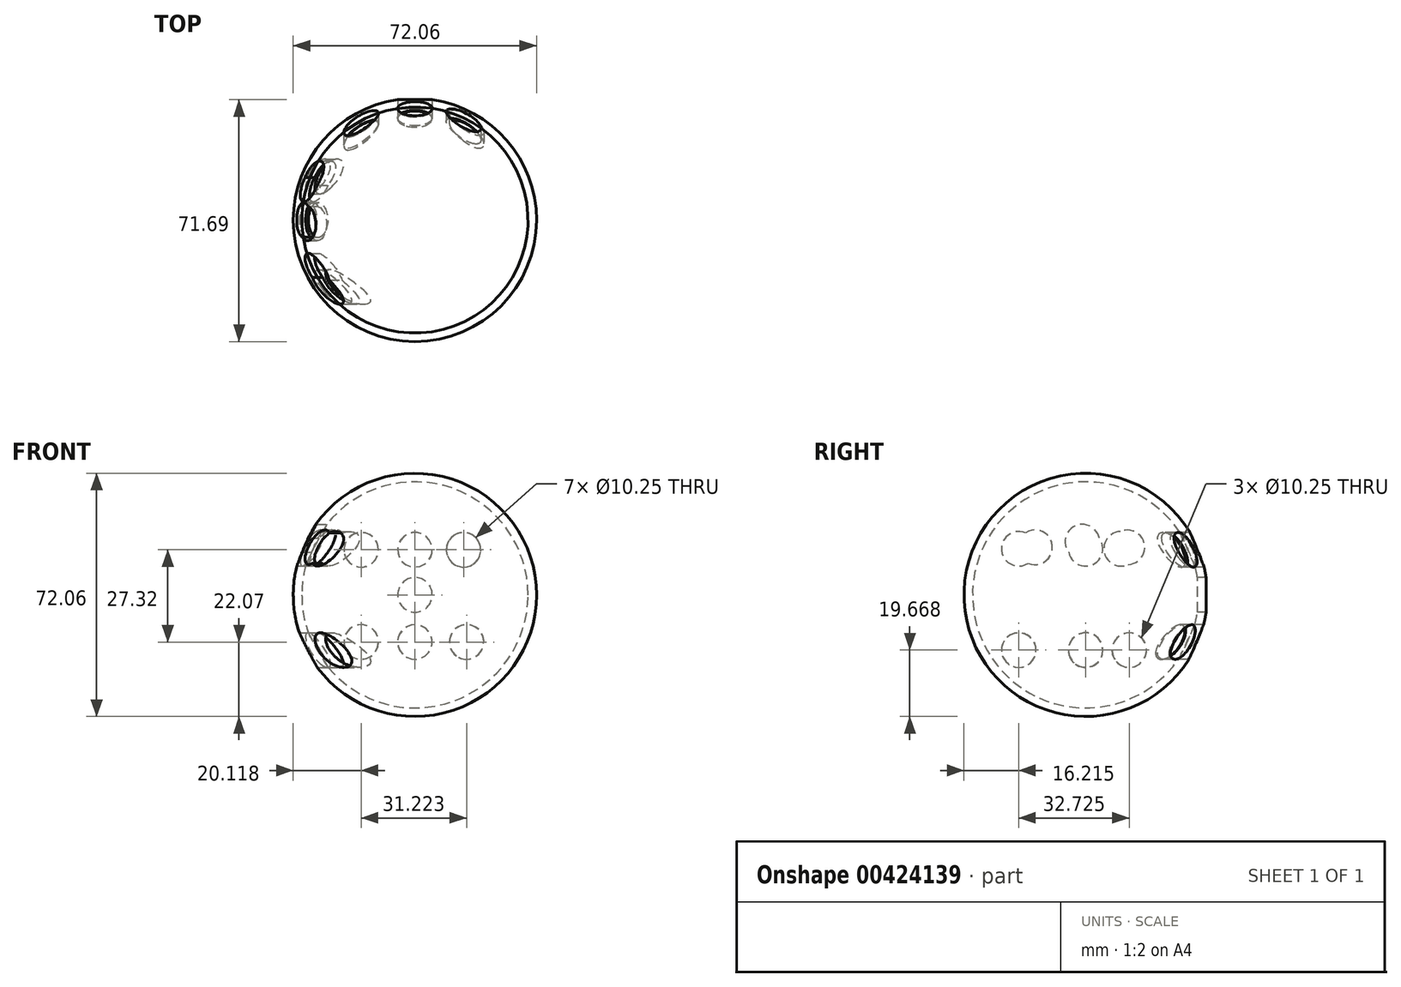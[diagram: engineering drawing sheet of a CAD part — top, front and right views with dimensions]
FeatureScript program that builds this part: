
annotation { "Feature Type Name" : "Feature", "Feature Type Description" : "" }
export const myFeature = defineFeature(function(context is Context, id is Id, definition is map)
    precondition{}
    {
        {
            var Q0;
            Q0=qCreatedBy(makeId("Front.planeOp"),FACE);
            var sketch = newSketch(context, id + "F0", { "sketchPlane" : qUnion([Q0])});
            skArc(sketch, "E0", {"start": v(-36.03, 0) * mm, "mid": v(0, -36.03) * mm, "end": v(36.03, 0) * mm});
            skLineSegment(sketch, "E1", {"start": v(-36.03, 0) * mm, "end": v(36.03, 0) * mm});
            skLineSegment(sketch, "E2", {"start": v(-57.34, 0) * mm, "end": v(54.04, 0) * mm, "construction": true});
            skSolve(sketch);
        }
        {
            var Q0;
            Q0=makeQuery(id+"F0.imprint","IMPRINT",FACE,{"disambiguationData":[TD([[makeQuery(id+"F0.imprint","IMPRINT",EDGE,{"derivedFrom":sQuery(id+"F0.wireOp",EDGE,"E0")}),1.0]])]});
            var Q1;
            Q1=sQuery(id+"F0.wireOp",EDGE,"E2");
            revolve(context, id + "F1", {"entities" : qUnion([Q0]), "axis" : qUnion([Q1]), "revolveType" : RevolveType.FULL});
        }
        {
            var Q0;
            Q0=qCreatedBy(makeId("Right.planeOp"),FACE);
            var sketch = newSketch(context, id + "F2", { "sketchPlane" : qUnion([Q0])});
            skFitSpline(sketch, "E3", {"points": [v(-56.14, 32.97) * mm, v(-60.08, 19.31) * mm, v(-56.14, 14.86) * mm, v(-52.5, 19.31) * mm, v(-56.14, 32.97) * mm]});
            skFitSpline(sketch, "E4", {"points": [v(-14.3, 24.87) * mm, v(-18.24, 11.21) * mm, v(-14.3, 6.76) * mm, v(-10.66, 11.21) * mm, v(-14.3, 24.87) * mm]});
            skFitSpline(sketch, "E5", {"points": [v(12.42, 24.87) * mm, v(8.48, 11.21) * mm, v(12.42, 6.76) * mm, v(16.06, 11.21) * mm, v(12.42, 24.87) * mm]});
            skFitSpline(sketch, "E6", {"points": [v(-0.8, 26.32) * mm, v(-4.73, 12.66) * mm, v(-0.8, 8.2) * mm, v(2.85, 12.66) * mm, v(-0.8, 26.32) * mm]});
            skPoint(sketch, "E7", {"position": v(12.35, 14.1) * mm});
            skPoint(sketch, "E8", {"position": v(-0.98, 15.77) * mm});
            skPoint(sketch, "E9", {"position": v(-14.96, 14.1) * mm});
            skSolve(sketch);
        }
        {
            var Q0;
            Q0=makeQuery(id+"F1.opRevolve","SWEPT_FACE",FACE,{"disambiguationData":[OSD([sQuery(id+"F0.wireOp",EDGE,"E0")])]});
            var Q1;
            Q1=makeQuery(id+"F1.opRevolve","SWEPT_BODY",BODY,{"disambiguationData":[OSD([sQuery(id+"F0.wireOp",EDGE,"E0"),sQuery(id+"F0.wireOp",EDGE,"E1")])]});
            shell(context, id + "F3", {"isHollow" : true, "entities" : qUnion([Q0]), "parts" : qUnion([Q1]), "thickness" : 2.54 * mm});
        }
        {
            var Q0;
            Q0=qCreatedBy(makeId("Front.planeOp"),FACE);
            var sketch = newSketch(context, id + "F4", { "sketchPlane" : qUnion([Q0])});
            skCircle(sketch, "E10", {"center": v(0, 0) * mm, "radius": 5.12 * mm});
            skSolve(sketch);
        }
        {
            var Q0;
            Q0=sQuery(id+"F4.wireOp",VERTEX,"E10.center");
            var Q1;
            Q1=makeQuery(id+"F1.opRevolve","SWEPT_BODY",BODY,{"disambiguationData":[OSD([sQuery(id+"F0.wireOp",EDGE,"E0"),sQuery(id+"F0.wireOp",EDGE,"E1")])]});
            hole(context, id + "F5", {"style" : HoleStyle.SIMPLE, "endStyle" : HoleEndStyle.THROUGH, "holeDiameter" : 10.25 * mm, "isTappedThrough" : true, "tappedDepth" : 12.7 * mm, "tapClearance" : 3, "startFromSketch" : true, "locations" : qUnion([Q0]), "scope" : qUnion([Q1])});
        }
        {
            var Q0;
            Q0=sQuery(id+"F2.wireOp",VERTEX,"E7");
            var Q1;
            Q1=sQuery(id+"F2.wireOp",VERTEX,"E8");
            var Q2;
            Q2=sQuery(id+"F2.wireOp",VERTEX,"E9");
            var Q3;
            Q3=makeQuery(id+"F1.opRevolve","SWEPT_BODY",BODY,{"disambiguationData":[OSD([sQuery(id+"F0.wireOp",EDGE,"E0"),sQuery(id+"F0.wireOp",EDGE,"E1")])]});
            hole(context, id + "F6", {"style" : HoleStyle.SIMPLE, "endStyle" : HoleEndStyle.THROUGH, "holeDiameter" : 10.25 * mm, "isTappedThrough" : true, "tappedDepth" : 12.7 * mm, "tapClearance" : 3, "startFromSketch" : true, "locations" : qUnion([Q0, Q1, Q2]), "scope" : qUnion([Q3])});
        }
        {
            var Q0;
            Q0=qCreatedBy(makeId("Front.planeOp"),FACE);
            var sketch = newSketch(context, id + "F7", { "sketchPlane" : qUnion([Q0])});
            skPoint(sketch, "E11", {"position": v(-15.91, 13.36) * mm});
            skPoint(sketch, "E12", {"position": v(0, 13.36) * mm});
            skPoint(sketch, "E13", {"position": v(14.41, 13.36) * mm});
            skPoint(sketch, "E14", {"position": v(15.31, -13.96) * mm});
            skPoint(sketch, "E15", {"position": v(0, -13.96) * mm});
            skPoint(sketch, "E16", {"position": v(-15.91, -13.96) * mm});
            skSolve(sketch);
        }
        {
            var Q0;
            Q0=sQuery(id+"F7.wireOp",VERTEX,"E11");
            var Q1;
            Q1=sQuery(id+"F7.wireOp",VERTEX,"E12");
            var Q2;
            Q2=sQuery(id+"F7.wireOp",VERTEX,"E13");
            var Q3;
            Q3=sQuery(id+"F7.wireOp",VERTEX,"E14");
            var Q4;
            Q4=sQuery(id+"F7.wireOp",VERTEX,"E15");
            var Q5;
            Q5=sQuery(id+"F7.wireOp",VERTEX,"E16");
            var Q6;
            Q6=makeQuery(id+"F1.opRevolve","SWEPT_BODY",BODY,{"disambiguationData":[OSD([sQuery(id+"F0.wireOp",EDGE,"E0"),sQuery(id+"F0.wireOp",EDGE,"E1")])]});
            hole(context, id + "F8", {"style" : HoleStyle.SIMPLE, "endStyle" : HoleEndStyle.THROUGH, "holeDiameter" : 10.25 * mm, "isTappedThrough" : true, "tappedDepth" : 12.7 * mm, "tapClearance" : 3, "startFromSketch" : true, "locations" : qUnion([Q0, Q1, Q2, Q3, Q4, Q5]), "scope" : qUnion([Q6])});
        }
        {
            var Q0;
            Q0=qCreatedBy(makeId("Right.planeOp"),FACE);
            var sketch = newSketch(context, id + "F9", { "sketchPlane" : qUnion([Q0])});
            skPoint(sketch, "E17", {"position": v(-19.81, 13.66) * mm});
            skPoint(sketch, "E18", {"position": v(0, 13.66) * mm});
            skPoint(sketch, "E19", {"position": v(10.5, 13.66) * mm});
            skPoint(sketch, "E20", {"position": v(12.9, -16.36) * mm});
            skPoint(sketch, "E21", {"position": v(0, -16.36) * mm});
            skPoint(sketch, "E22", {"position": v(-19.81, -16.36) * mm});
            skSolve(sketch);
        }
        {
            var Q0;
            Q0=sQuery(id+"F9.wireOp",VERTEX,"E17");
            var Q1;
            Q1=sQuery(id+"F9.wireOp",VERTEX,"E18");
            var Q2;
            Q2=sQuery(id+"F9.wireOp",VERTEX,"E19");
            var Q3;
            Q3=sQuery(id+"F9.wireOp",VERTEX,"E20");
            var Q4;
            Q4=sQuery(id+"F9.wireOp",VERTEX,"E21");
            var Q5;
            Q5=sQuery(id+"F9.wireOp",VERTEX,"E22");
            var Q6;
            Q6=makeQuery(id+"F1.opRevolve","SWEPT_BODY",BODY,{"disambiguationData":[OSD([sQuery(id+"F0.wireOp",EDGE,"E0"),sQuery(id+"F0.wireOp",EDGE,"E1")])]});
            hole(context, id + "F10", {"style" : HoleStyle.SIMPLE, "endStyle" : HoleEndStyle.THROUGH, "holeDiameter" : 10.25 * mm, "isTappedThrough" : true, "tappedDepth" : 12.7 * mm, "tapClearance" : 3, "startFromSketch" : true, "locations" : qUnion([Q0, Q1, Q2, Q3, Q4, Q5]), "scope" : qUnion([Q6])});
        }
    });
